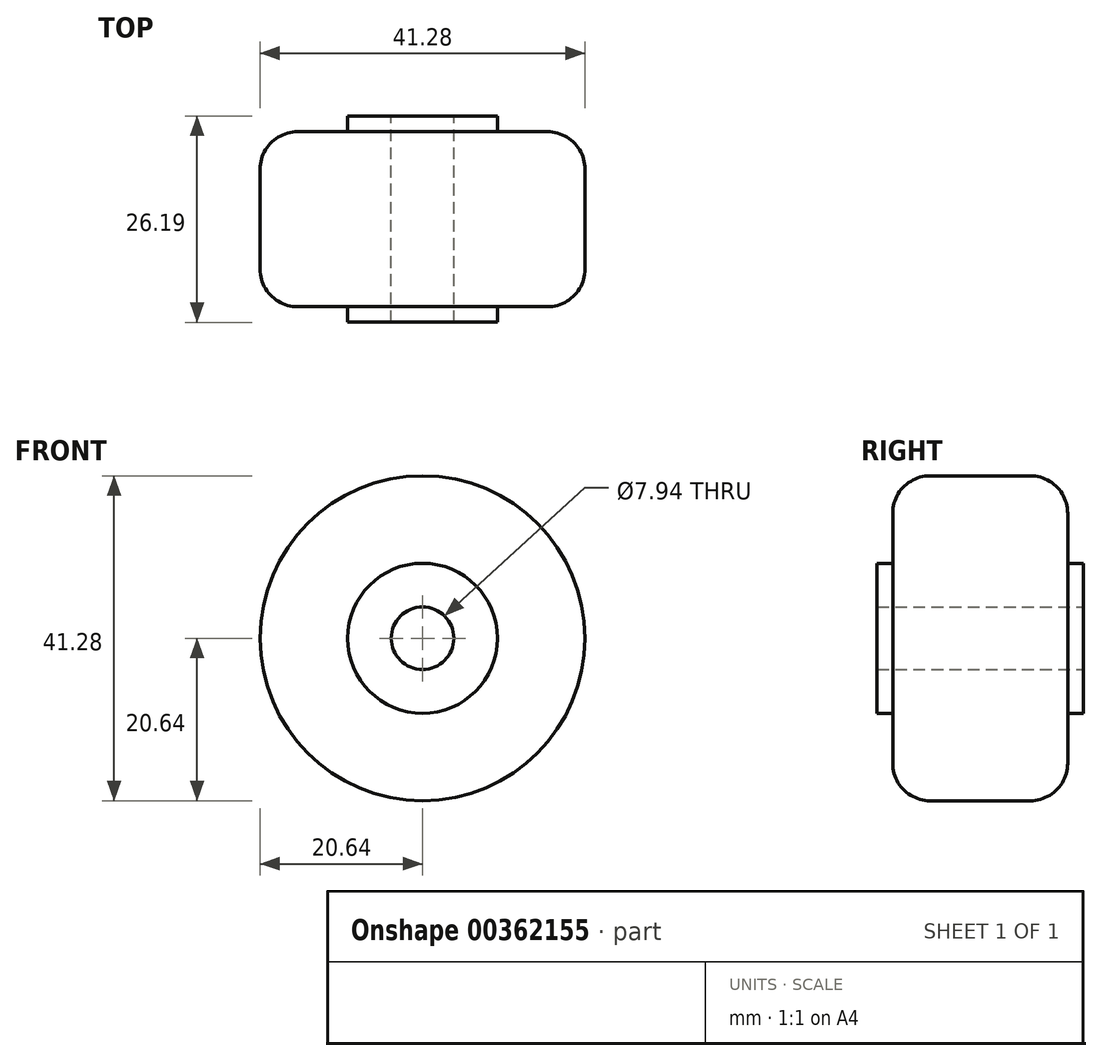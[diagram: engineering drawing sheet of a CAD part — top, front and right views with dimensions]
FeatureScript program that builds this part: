
annotation { "Feature Type Name" : "Feature", "Feature Type Description" : "" }
export const myFeature = defineFeature(function(context is Context, id is Id, definition is map)
    precondition{}
    {
        {
            var Q0;
            Q0=qCreatedBy(makeId("Front.planeOp"),FACE);
            var sketch = newSketch(context, id + "F0", { "sketchPlane" : qUnion([Q0])});
            skCircle(sketch, "E0", {"center": v(0, 0) * mm, "radius": 20.64 * mm});
            skSolve(sketch);
        }
        {
            var Q0;
            Q0=makeQuery(id+"F0.imprint","IMPRINT",FACE,{"disambiguationData":[TD([[makeQuery(id+"F0.imprint","IMPRINT",EDGE,{"derivedFrom":sQuery(id+"F0.wireOp",EDGE,"E0")}),1.0]])]});
            var Q1;
            Q1=makeQuery(id+"F0.imprint","IMPRINT",FACE,{"disambiguationData":[TD([[makeQuery(id+"F0.imprint","IMPRINT",EDGE,{"derivedFrom":sQuery(id+"F0.wireOp",EDGE,"rTpFH4oF-Fhsw-xrx9-W9MS-0q15H7L1GDHe")}),1.0]])]});
            extrude(context, id + "F1", {"entities" : qUnion([Q0, Q1]), "depth" : 22.22 * mm});
        }
        {
            var Q0;
            Q0=sQuery(id+"F0.wireOp",VERTEX,"E0.center");
            var Q1;
            Q1=makeQuery(id+"F1.opExtrude","SWEPT_BODY",BODY,{"disambiguationData":[OSD([sQuery(id+"F0.wireOp",EDGE,"E0")])]});
            hole(context, id + "F2", {"style" : HoleStyle.SIMPLE, "endStyle" : HoleEndStyle.THROUGH, "oppositeDirection" : true, "holeDiameter" : 7.94 * mm, "isTappedThrough" : true, "tappedDepth" : 12.7 * mm, "tapClearance" : 3, "startFromSketch" : true, "locations" : qUnion([Q0]), "scope" : qUnion([Q1])});
        }
        {
            var Q0;
            Q0=makeQuery(id+"F1.opExtrude","CAP_EDGE",EDGE,{"disambiguationData":[OSD([sQuery(id+"F0.wireOp",EDGE,"E0")])],"isStart":false});
            var Q1;
            Q1=makeQuery(id+"F1.opExtrude","CAP_EDGE",EDGE,{"disambiguationData":[OSD([sQuery(id+"F0.wireOp",EDGE,"E0")])],"isStart":true});
            fillet(context, id + "F3", {"entities" : qUnion([Q0, Q1]), "radius" : 4.76 * mm, "tangentPropagation" : true, "allowEdgeOverflow" : false});
        }
        {
            var Q0;
            Q0=makeQuery(id+"F1.opExtrude","CAP_FACE",FACE,{"disambiguationData":[OSD([sQuery(id+"F0.wireOp",EDGE,"E0")])],"isStart":false});
            var sketch = newSketch(context, id + "F4", { "sketchPlane" : qUnion([Q0])});
            skCircle(sketch, "E1.0", {"center": v(0, 0) * mm, "radius": 3.97 * mm});
            skCircle(sketch, "E2", {"center": v(0, 0) * mm, "radius": 9.53 * mm});
            skSolve(sketch);
        }
        {
            var Q0;
            Q0 = qSketchRegion(id + "F4", true);
            extrude(context, id + "F5", {"entities" : qUnion([Q0]), "operationType" : NewBodyOperationType.ADD, "depth" : 1.98 * mm});
        }
        {
            var Q0;
            Q0=makeQuery(id+"F0.imprint","IMPRINT",FACE,{"disambiguationData":[TD([[makeQuery(id+"F0.imprint","IMPRINT",EDGE,{"derivedFrom":sQuery(id+"F0.wireOp",EDGE,"E0")}),1.0]])]});
            var sketch = newSketch(context, id + "F6", { "sketchPlane" : qUnion([Q0])});
            skCircle(sketch, "E3", {"center": v(0, 0) * mm, "radius": 9.53 * mm});
            skCircle(sketch, "E4.0", {"center": v(0, 0) * mm, "radius": 3.97 * mm});
            skSolve(sketch);
        }
        {
            var Q0;
            Q0=makeQuery(id+"F6.imprint","IMPRINT",FACE,{"disambiguationData":[TD([[makeQuery(id+"F6.imprint","IMPRINT",EDGE,{"derivedFrom":sQuery(id+"F6.wireOp",EDGE,"E3")}),1.0]])]});
            extrude(context, id + "F7", {"entities" : qUnion([Q0]), "operationType" : NewBodyOperationType.ADD, "oppositeDirection" : true, "depth" : 1.98 * mm});
        }
    });
